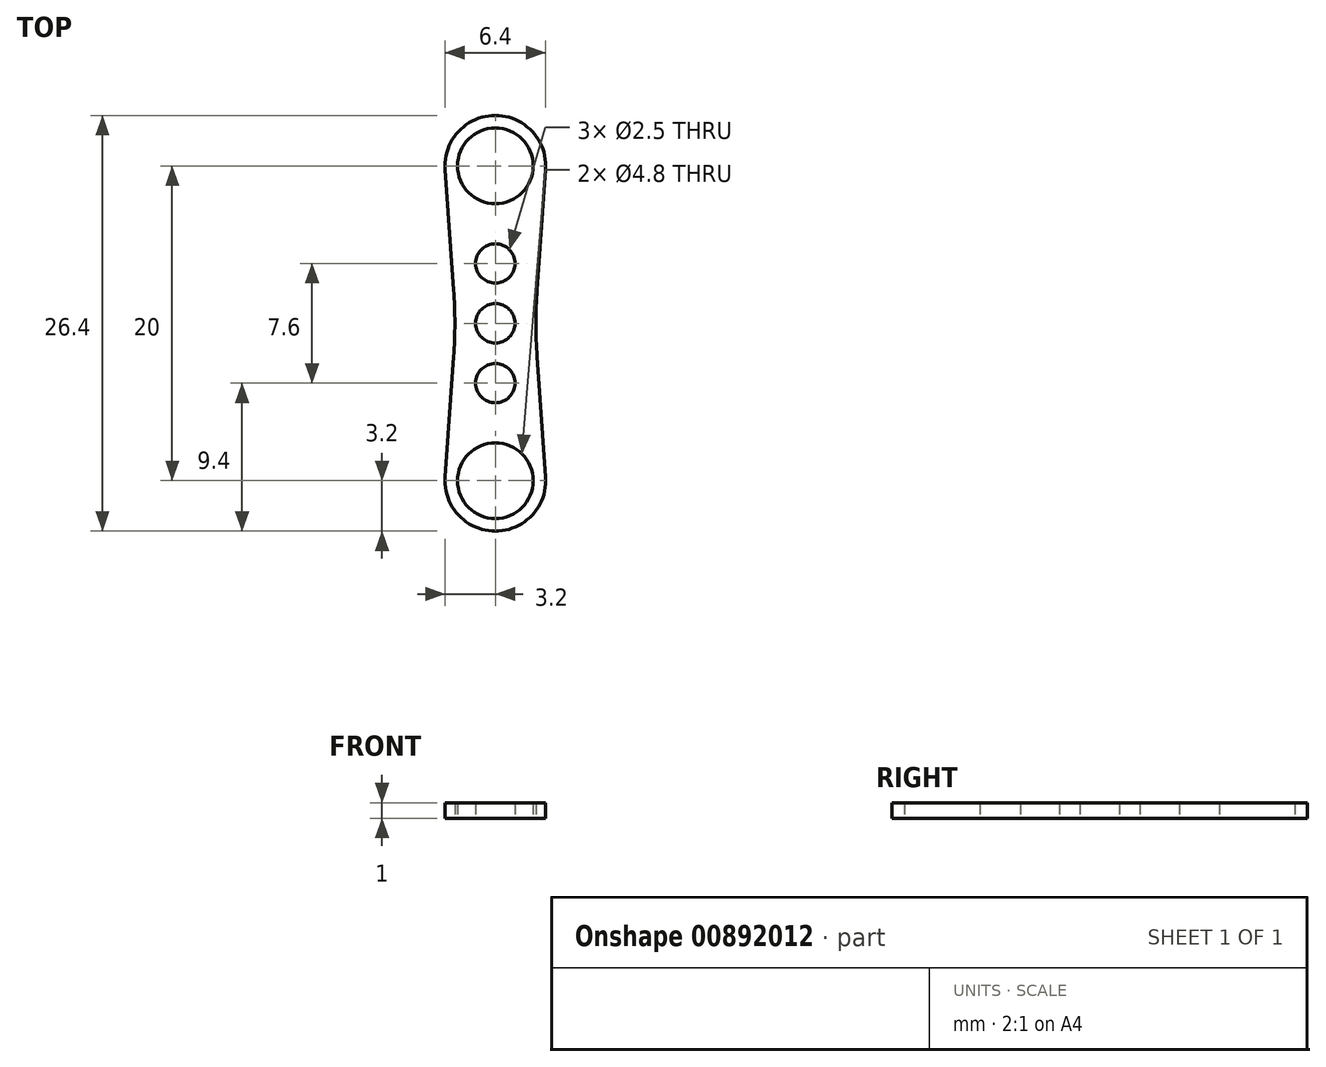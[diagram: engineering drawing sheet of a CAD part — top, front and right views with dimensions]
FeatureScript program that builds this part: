
annotation { "Feature Type Name" : "Feature", "Feature Type Description" : "" }
export const myFeature = defineFeature(function(context is Context, id is Id, definition is map)
    precondition{}
    {
        {
            var Q0;
            Q0=qCreatedBy(makeId("Top.planeOp"),FACE);
            var sketch = newSketch(context, id + "F0", { "sketchPlane" : qUnion([Q0])});
            skCircle(sketch, "E0", {"center": v(0, 0) * mm, "radius": 2.4 * mm});
            skLineSegment(sketch, "E1", {"start": v(0, 0) * mm, "end": v(0, 20) * mm});
            skCircle(sketch, "E2", {"center": v(0, 20) * mm, "radius": 2.4 * mm});
            skArc(sketch, "E3", {"start": v(-3.2, 0.23) * mm, "mid": v(0, -3.2) * mm, "end": v(3.2, 0.23) * mm});
            skArc(sketch, "E4", {"start": v(3.2, 19.77) * mm, "mid": v(0, 23.2) * mm, "end": v(-3.2, 19.77) * mm});
            skLineSegment(sketch, "E5", {"start": v(0, 10) * mm, "end": v(-2.5, 10) * mm});
            skLineSegment(sketch, "E6", {"start": v(-2.65, 7.88) * mm, "end": v(-3.2, 0.23) * mm});
            skLineSegment(sketch, "E7.MirrorCS", {"start": v(-2.65, 12.12) * mm, "end": v(-3.2, 19.77) * mm});
            skPoint(sketch, "E8.visualSharp", {"position": v(-2.5, 10) * mm});
            skArc(sketch, "E8.filletArc", {"start": v(-2.65, 7.88) * mm, "mid": v(-2.58, 10) * mm, "end": v(-2.65, 12.12) * mm});
            skLineSegment(sketch, "E9.MirrorCS", {"start": v(2.65, 12.12) * mm, "end": v(3.2, 19.77) * mm});
            skArc(sketch, "E10.MirrorCS", {"start": v(2.65, 7.88) * mm, "mid": v(2.58, 10) * mm, "end": v(2.65, 12.12) * mm});
            skLineSegment(sketch, "E11.MirrorCS", {"start": v(2.65, 7.88) * mm, "end": v(3.2, 0.23) * mm});
            skCircle(sketch, "E12", {"center": v(0, 10) * mm, "radius": 1.25 * mm});
            skLineSegment(sketch, "E13", {"start": v(0, 10) * mm, "end": v(0, 17.6) * mm});
            skCircle(sketch, "E14", {"center": v(0, 13.8) * mm, "radius": 1.25 * mm});
            skCircle(sketch, "E15.MirrorC", {"center": v(0, 6.2) * mm, "radius": 1.25 * mm});
            skSolve(sketch);
        }
        {
            var Q0;
            Q0 = qSketchRegion(id + "F0", true);
            extrude(context, id + "F1", {"entities" : qUnion([Q0]), "depth" : 1 * mm, "offsetDistance" : 25 * mm});
        }
    });
